# Revit family: Deca_Desviador luxo para chuveiro 330mm_Banho Luxo_1982.LUX.330
name_source: partatom
category: Plumbing Fixtures
units: mm (PartAtom-declared; Revit-internal decimal feet)

## family parameters
Cut with Voids When Loaded = No
Host = Face
Part Type = Normal
Room Calculation Point = No
Round Connector Dimension = Use Radius
Shared = No

## types (6) — shared parameters
Acompanha o Produto = Acompanha Parafuso e bucha para fixação
Aprovado por = quattroD
Atendimento ao Cliente = 0800-0117073
Categoria = CHUVEIROS E DUCHAS
Composição Anel Vedação = -
Composição Assento = -
Composição Componente = -
Consumo = -
Cor Interna = -
Cor Secundária = -
Cores Componente = -
Criado por = quattroD
Código Pai = 1982.LUX.330
Default Elevation = 2000 mm
Description = Desviador luxo para chuveiro 330mm
Diâmetro Água Fria = 15 mm  [stored 0.0492126 ft]
Informações Complementares = -
Itens de Instalação = -
Linha = Banho Luxo
Manufacturer = Deca
Norma = Não Possui
Pressão máx. funcionamento = 40 MCA
Pressão mín. Aquec. Acúmulo = 4 MCA
Pressão mín. Aquec. Passagem = 8 MCA
Pressão mín. funcionamento = 4 MCA
Raio Água Fria = 8 mm  [stored 0.0262467 ft]
Saída de Esgoto = -
Segmento = Banheiro Luxo
Tipo de dispositivo economizador = -
Tipo de mecanismo utilizado = -
Tipo de rosca de entrada = BSP NBR 8133
Tipo de rosca de saída = -
URL = www.deca.com.br
Vazão na Pressão máx. (L/min) = -
Vazão na Pressão mín. (L/min) = -
zero-valued in all types: CWFU

## per-type parameters (varying)
| type | Composição Básica | Cor Principal | Material | Model | Peso Líquido (Kg) |
| 1982.C.LUX.330_Cromado | Liga cobre (bronze e latão),Aço,Plástico de Engenharia,Elastômeros | Cromado | Deca_Cromado | 1982.C.LUX.330 | 1.82 |
| 1982.BL.LUX.330.MT_Black Matte | Liga de Cobre (bronze e latão),Plásticos de Engenharia,Elastômeros | Black Matte | Deca_Black Matte | 1982.BL.LUX.330.MT | 2.651 |
| 1982.BL.LUX.330.NO_Black Noir | Liga cobre (bronze e latão),Aço,Plástico de Engenharia,Elastômeros | Black Noir | Deca_Black Noir | 1982.BL.LUX.330.NO | 2.264 |
| 1982.CT.LUX.330.MT_Corten | Liga de Cobre (bronze e latão),Plásticos de Engenharia,Elastômeros | Corten | Deca_Corten | 1982.CT.LUX.330.MT | 2.802 |
| 1982.GL.LUX.330.MT_Gold Matte | Liga de Cobre (bronze e latão),Plásticos de Engenharia,Elastômeros | Gold Matte | Deca_Gold Matte | 1982.GL.LUX.330.MT | 2.651 |
| 1982.GL.LUX.330.RD_Red Gold | Liga cobre (bronze e latão),Aço,Plástico de Engenharia,Elastômeros | Red Gold | Deca_Red Gold | 1982.GL.LUX.330.RD | 2.264 |

note: [stored X ft] marks values corroborated as IEEE doubles in the binary element streams (Revit-internal decimal feet)

## geometry (parser evidence)
native form markers: Sweep x2
no freeform markers — native parametric forms only
